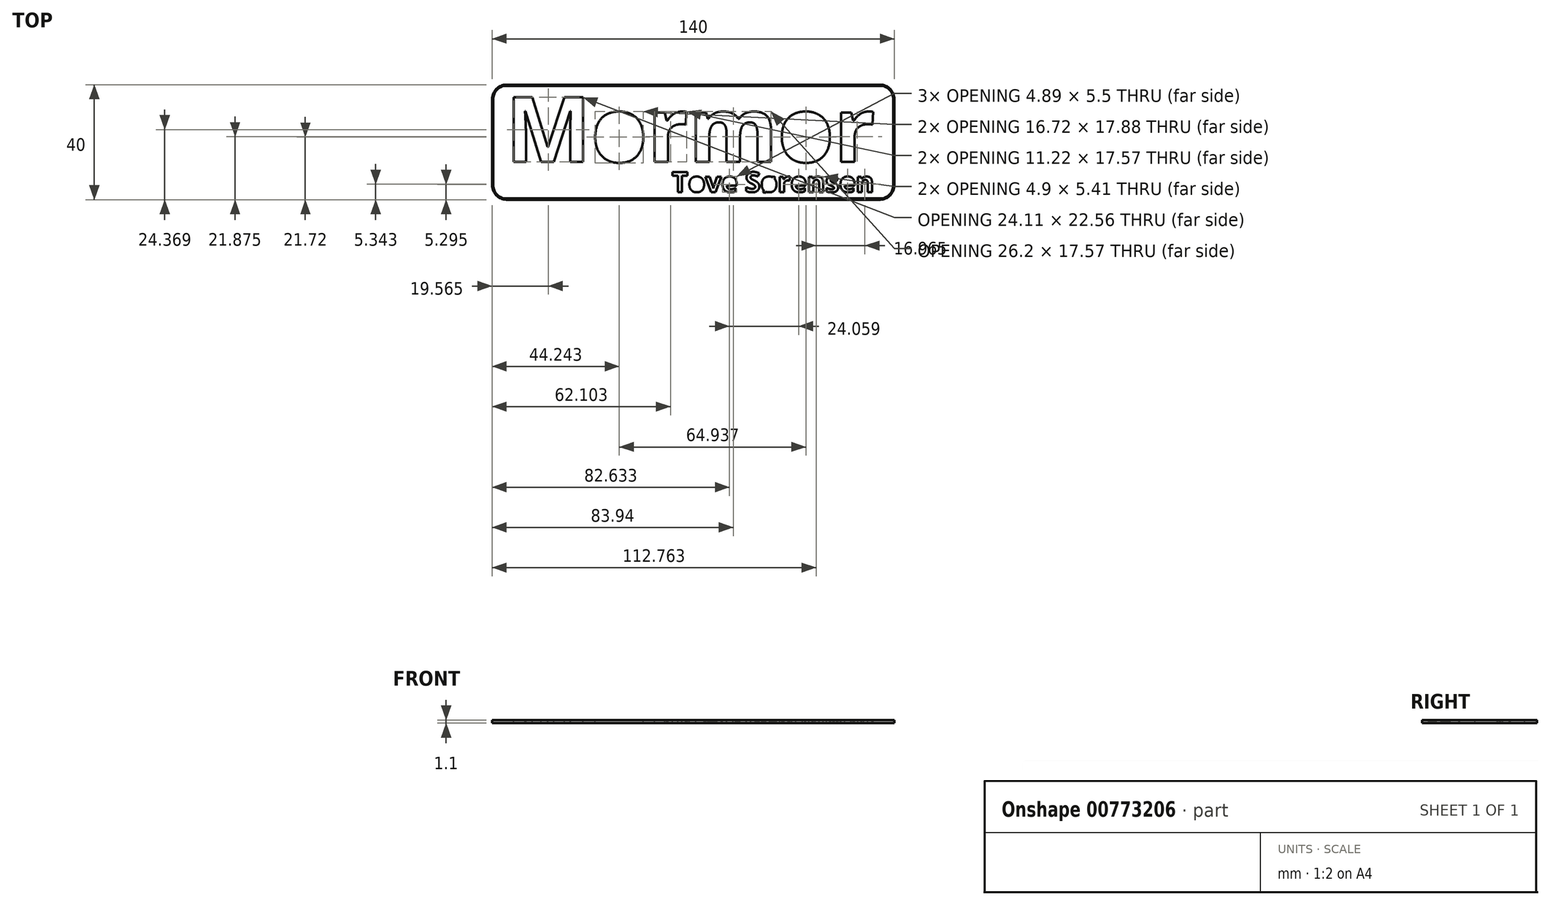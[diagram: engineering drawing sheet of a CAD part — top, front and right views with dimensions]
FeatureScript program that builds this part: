
annotation { "Feature Type Name" : "Feature", "Feature Type Description" : "" }
export const myFeature = defineFeature(function(context is Context, id is Id, definition is map)
    precondition{}
    {
        {
            var Q0;
            Q0=qCreatedBy(makeId("Top.planeOp"),FACE);
            var sketch = newSketch(context, id + "F0", { "sketchPlane" : qUnion([Q0])});
            skLineSegment(sketch, "E0.bottom", {"start": v(-65.25, 40) * mm, "end": v(74.75, 40) * mm});
            skLineSegment(sketch, "E0.top", {"start": v(-65.25, 0) * mm, "end": v(74.75, 0) * mm});
            skLineSegment(sketch, "E0.left", {"start": v(-65.25, 40) * mm, "end": v(-65.25, 0) * mm});
            skLineSegment(sketch, "E0.right", {"start": v(74.75, 40) * mm, "end": v(74.75, 0) * mm});
            skText(sketch, "E1", { "text": "Mormor", "fontName": "OpenSans-Bold.ttf"});
            skText(sketch, "E2", { "text": "Tove Sørensen", "fontName": "OpenSans-Bold.ttf"});
            const initialGuessF0  = {"E1": [-0.06058, 0.01309, 1, 0, 0.02275], "E2": [-0.00268, 0.00264, 1, 0, 0.007]};
            skSetInitialGuess(sketch, initialGuessF0);
            skSolve(sketch);
        }
        {
            var Q0;
            Q0=makeQuery(id+"F0.imprint","IMPRINT",FACE,{"disambiguationData":[TD([[makeQuery(id+"F0.imprint","IMPRINT",EDGE,{"derivedFrom":sQuery(id+"F0.wireOp",EDGE,"E0.bottom")}),-1.0]])]});
            var Q1;
            Q1=makeQuery(id+"F0.imprint","IMPRINT",FACE,{"disambiguationData":[TD([[makeQuery(id+"F0.imprint","IMPRINT",EDGE,{"derivedFrom":sQuery(id+"F0.wireOp",EDGE,"E1.sketch_text.stroke-0")}),1.0]])]});
            extrude(context, id + "F1", {"entities" : qUnion([Q0, Q1]), "oppositeDirection" : true, "depth" : 1 * mm, "offsetDistance" : 25 * mm});
        }
        {
            var Q0;
            Q0=makeQuery(id+"F1.opExtrude","SWEPT_EDGE",EDGE,{"disambiguationData":[OSD([sQuery(id+"F0.wireOp",EDGE,"E0.top"),sQuery(id+"F0.wireOp",EDGE,"E0.right")])]});
            var Q1;
            Q1=makeQuery(id+"F1.opExtrude","SWEPT_EDGE",EDGE,{"disambiguationData":[OSD([sQuery(id+"F0.wireOp",EDGE,"E0.top"),sQuery(id+"F0.wireOp",EDGE,"E0.left")])]});
            var Q2;
            Q2=makeQuery(id+"F1.opExtrude","SWEPT_EDGE",EDGE,{"disambiguationData":[OSD([sQuery(id+"F0.wireOp",EDGE,"E0.bottom"),sQuery(id+"F0.wireOp",EDGE,"E0.left")])]});
            var Q3;
            Q3=makeQuery(id+"F1.opExtrude","SWEPT_EDGE",EDGE,{"disambiguationData":[OSD([sQuery(id+"F0.wireOp",EDGE,"E0.bottom"),sQuery(id+"F0.wireOp",EDGE,"E0.right")])]});
            fillet(context, id + "F2", {"entities" : qUnion([Q0, Q1, Q2, Q3]), "radius" : 5 * mm, "tangentPropagation" : true, "allowEdgeOverflow" : false});
        }
        {
            var Q0;
            Q0=makeQuery(id+"F1.opExtrude","CAP_FACE",FACE,{"disambiguationData":[OSD([sQuery(id+"F0.wireOp",EDGE,"E0.bottom"),sQuery(id+"F0.wireOp",EDGE,"E0.top"),sQuery(id+"F0.wireOp",EDGE,"E0.left"),sQuery(id+"F0.wireOp",EDGE,"E0.right"),sQuery(id+"F0.wireOp",EDGE,"E1.sketch_text.stroke-0"),sQuery(id+"F0.wireOp",EDGE,"E1.sketch_text.stroke-1"),sQuery(id+"F0.wireOp",EDGE,"E1.sketch_text.stroke-2"),sQuery(id+"F0.wireOp",EDGE,"E1.sketch_text.stroke-3"),sQuery(id+"F0.wireOp",EDGE,"E1.sketch_text.stroke-4"),sQuery(id+"F0.wireOp",EDGE,"E1.sketch_text.stroke-5"),sQuery(id+"F0.wireOp",EDGE,"E1.sketch_text.stroke-6"),sQuery(id+"F0.wireOp",EDGE,"E1.sketch_text.stroke-7"),sQuery(id+"F0.wireOp",EDGE,"E1.sketch_text.stroke-8"),sQuery(id+"F0.wireOp",EDGE,"E1.sketch_text.stroke-9"),sQuery(id+"F0.wireOp",EDGE,"E1.sketch_text.stroke-10"),sQuery(id+"F0.wireOp",EDGE,"E1.sketch_text.stroke-11"),sQuery(id+"F0.wireOp",EDGE,"E1.sketch_text.stroke-12"),sQuery(id+"F0.wireOp",EDGE,"E1.sketch_text.stroke-13"),sQuery(id+"F0.wireOp",EDGE,"E1.sketch_text.stroke-14"),sQuery(id+"F0.wireOp",EDGE,"E1.sketch_text.stroke-15"),sQuery(id+"F0.wireOp",EDGE,"E1.sketch_text.stroke-16"),sQuery(id+"F0.wireOp",EDGE,"E1.sketch_text.stroke-17"),sQuery(id+"F0.wireOp",EDGE,"E1.sketch_text.stroke-18"),sQuery(id+"F0.wireOp",EDGE,"E1.sketch_text.stroke-27"),sQuery(id+"F0.wireOp",EDGE,"E1.sketch_text.stroke-28"),sQuery(id+"F0.wireOp",EDGE,"E1.sketch_text.stroke-29"),sQuery(id+"F0.wireOp",EDGE,"E1.sketch_text.stroke-30"),sQuery(id+"F0.wireOp",EDGE,"E1.sketch_text.stroke-31"),sQuery(id+"F0.wireOp",EDGE,"E1.sketch_text.stroke-32"),sQuery(id+"F0.wireOp",EDGE,"E1.sketch_text.stroke-33"),sQuery(id+"F0.wireOp",EDGE,"E1.sketch_text.stroke-34"),sQuery(id+"F0.wireOp",EDGE,"E1.sketch_text.stroke-35"),sQuery(id+"F0.wireOp",EDGE,"E1.sketch_text.stroke-36"),sQuery(id+"F0.wireOp",EDGE,"E1.sketch_text.stroke-37"),sQuery(id+"F0.wireOp",EDGE,"E1.sketch_text.stroke-38"),sQuery(id+"F0.wireOp",EDGE,"E1.sketch_text.stroke-39"),sQuery(id+"F0.wireOp",EDGE,"E1.sketch_text.stroke-40"),sQuery(id+"F0.wireOp",EDGE,"E1.sketch_text.stroke-41"),sQuery(id+"F0.wireOp",EDGE,"E1.sketch_text.stroke-42"),sQuery(id+"F0.wireOp",EDGE,"E1.sketch_text.stroke-43"),sQuery(id+"F0.wireOp",EDGE,"E1.sketch_text.stroke-44"),sQuery(id+"F0.wireOp",EDGE,"E1.sketch_text.stroke-45"),sQuery(id+"F0.wireOp",EDGE,"E1.sketch_text.stroke-46"),sQuery(id+"F0.wireOp",EDGE,"E1.sketch_text.stroke-47"),sQuery(id+"F0.wireOp",EDGE,"E1.sketch_text.stroke-48"),sQuery(id+"F0.wireOp",EDGE,"E1.sketch_text.stroke-49"),sQuery(id+"F0.wireOp",EDGE,"E1.sketch_text.stroke-50"),sQuery(id+"F0.wireOp",EDGE,"E1.sketch_text.stroke-51"),sQuery(id+"F0.wireOp",EDGE,"E1.sketch_text.stroke-52"),sQuery(id+"F0.wireOp",EDGE,"E1.sketch_text.stroke-53"),sQuery(id+"F0.wireOp",EDGE,"E1.sketch_text.stroke-54"),sQuery(id+"F0.wireOp",EDGE,"E1.sketch_text.stroke-55"),sQuery(id+"F0.wireOp",EDGE,"E1.sketch_text.stroke-56"),sQuery(id+"F0.wireOp",EDGE,"E1.sketch_text.stroke-57"),sQuery(id+"F0.wireOp",EDGE,"E1.sketch_text.stroke-58"),sQuery(id+"F0.wireOp",EDGE,"E1.sketch_text.stroke-59"),sQuery(id+"F0.wireOp",EDGE,"E1.sketch_text.stroke-60"),sQuery(id+"F0.wireOp",EDGE,"E1.sketch_text.stroke-61"),sQuery(id+"F0.wireOp",EDGE,"E1.sketch_text.stroke-62"),sQuery(id+"F0.wireOp",EDGE,"E1.sketch_text.stroke-63"),sQuery(id+"F0.wireOp",EDGE,"E1.sketch_text.stroke-64"),sQuery(id+"F0.wireOp",EDGE,"E1.sketch_text.stroke-65"),sQuery(id+"F0.wireOp",EDGE,"E1.sketch_text.stroke-66"),sQuery(id+"F0.wireOp",EDGE,"E1.sketch_text.stroke-67"),sQuery(id+"F0.wireOp",EDGE,"E1.sketch_text.stroke-68"),sQuery(id+"F0.wireOp",EDGE,"E1.sketch_text.stroke-69"),sQuery(id+"F0.wireOp",EDGE,"E1.sketch_text.stroke-70"),sQuery(id+"F0.wireOp",EDGE,"E1.sketch_text.stroke-71"),sQuery(id+"F0.wireOp",EDGE,"E1.sketch_text.stroke-72"),sQuery(id+"F0.wireOp",EDGE,"E1.sketch_text.stroke-73"),sQuery(id+"F0.wireOp",EDGE,"E1.sketch_text.stroke-74"),sQuery(id+"F0.wireOp",EDGE,"E1.sketch_text.stroke-75"),sQuery(id+"F0.wireOp",EDGE,"E1.sketch_text.stroke-76"),sQuery(id+"F0.wireOp",EDGE,"E1.sketch_text.stroke-77"),sQuery(id+"F0.wireOp",EDGE,"E1.sketch_text.stroke-86"),sQuery(id+"F0.wireOp",EDGE,"E1.sketch_text.stroke-87"),sQuery(id+"F0.wireOp",EDGE,"E1.sketch_text.stroke-88"),sQuery(id+"F0.wireOp",EDGE,"E1.sketch_text.stroke-89"),sQuery(id+"F0.wireOp",EDGE,"E1.sketch_text.stroke-90"),sQuery(id+"F0.wireOp",EDGE,"E1.sketch_text.stroke-91"),sQuery(id+"F0.wireOp",EDGE,"E1.sketch_text.stroke-92"),sQuery(id+"F0.wireOp",EDGE,"E1.sketch_text.stroke-93"),sQuery(id+"F0.wireOp",EDGE,"E1.sketch_text.stroke-94"),sQuery(id+"F0.wireOp",EDGE,"E1.sketch_text.stroke-95"),sQuery(id+"F0.wireOp",EDGE,"E1.sketch_text.stroke-96"),sQuery(id+"F0.wireOp",EDGE,"E1.sketch_text.stroke-97"),sQuery(id+"F0.wireOp",EDGE,"E1.sketch_text.stroke-98"),sQuery(id+"F0.wireOp",EDGE,"E1.sketch_text.stroke-99"),sQuery(id+"F0.wireOp",EDGE,"E1.sketch_text.stroke-100"),sQuery(id+"F0.wireOp",EDGE,"E1.sketch_text.stroke-101"),sQuery(id+"F0.wireOp",EDGE,"E1.sketch_text.stroke-102"),sQuery(id+"F0.wireOp",EDGE,"E1.sketch_text.stroke-103"),sQuery(id+"F0.wireOp",EDGE,"E1.sketch_text.stroke-104"),sQuery(id+"F0.wireOp",EDGE,"E1.sketch_text.stroke-105"),sQuery(id+"F0.wireOp",EDGE,"E1.sketch_text.stroke-106"),sQuery(id+"F0.wireOp",EDGE,"E1.sketch_text.stroke-107"),sQuery(id+"F0.wireOp",EDGE,"E1.sketch_text.stroke-108"),sQuery(id+"F0.wireOp",EDGE,"E2.sketch_text.stroke-0"),sQuery(id+"F0.wireOp",EDGE,"E2.sketch_text.stroke-1"),sQuery(id+"F0.wireOp",EDGE,"E2.sketch_text.stroke-2"),sQuery(id+"F0.wireOp",EDGE,"E2.sketch_text.stroke-3"),sQuery(id+"F0.wireOp",EDGE,"E2.sketch_text.stroke-4"),sQuery(id+"F0.wireOp",EDGE,"E2.sketch_text.stroke-5"),sQuery(id+"F0.wireOp",EDGE,"E2.sketch_text.stroke-6"),sQuery(id+"F0.wireOp",EDGE,"E2.sketch_text.stroke-7"),sQuery(id+"F0.wireOp",EDGE,"E2.sketch_text.stroke-16"),sQuery(id+"F0.wireOp",EDGE,"E2.sketch_text.stroke-17"),sQuery(id+"F0.wireOp",EDGE,"E2.sketch_text.stroke-18"),sQuery(id+"F0.wireOp",EDGE,"E2.sketch_text.stroke-19"),sQuery(id+"F0.wireOp",EDGE,"E2.sketch_text.stroke-20"),sQuery(id+"F0.wireOp",EDGE,"E2.sketch_text.stroke-21"),sQuery(id+"F0.wireOp",EDGE,"E2.sketch_text.stroke-22"),sQuery(id+"F0.wireOp",EDGE,"E2.sketch_text.stroke-23"),sQuery(id+"F0.wireOp",EDGE,"E2.sketch_text.stroke-24"),sQuery(id+"F0.wireOp",EDGE,"E2.sketch_text.stroke-25"),sQuery(id+"F0.wireOp",EDGE,"E2.sketch_text.stroke-26"),sQuery(id+"F0.wireOp",EDGE,"E2.sketch_text.stroke-27"),sQuery(id+"F0.wireOp",EDGE,"E2.sketch_text.stroke-28"),sQuery(id+"F0.wireOp",EDGE,"E2.sketch_text.stroke-29"),sQuery(id+"F0.wireOp",EDGE,"E2.sketch_text.stroke-30"),sQuery(id+"F0.wireOp",EDGE,"E2.sketch_text.stroke-31"),sQuery(id+"F0.wireOp",EDGE,"E2.sketch_text.stroke-32"),sQuery(id+"F0.wireOp",EDGE,"E2.sketch_text.stroke-33"),sQuery(id+"F0.wireOp",EDGE,"E2.sketch_text.stroke-34"),sQuery(id+"F0.wireOp",EDGE,"E2.sketch_text.stroke-35"),sQuery(id+"F0.wireOp",EDGE,"E2.sketch_text.stroke-41"),sQuery(id+"F0.wireOp",EDGE,"E2.sketch_text.stroke-42"),sQuery(id+"F0.wireOp",EDGE,"E2.sketch_text.stroke-43"),sQuery(id+"F0.wireOp",EDGE,"E2.sketch_text.stroke-44"),sQuery(id+"F0.wireOp",EDGE,"E2.sketch_text.stroke-45"),sQuery(id+"F0.wireOp",EDGE,"E2.sketch_text.stroke-46"),sQuery(id+"F0.wireOp",EDGE,"E2.sketch_text.stroke-47"),sQuery(id+"F0.wireOp",EDGE,"E2.sketch_text.stroke-48"),sQuery(id+"F0.wireOp",EDGE,"E2.sketch_text.stroke-49"),sQuery(id+"F0.wireOp",EDGE,"E2.sketch_text.stroke-50"),sQuery(id+"F0.wireOp",EDGE,"E2.sketch_text.stroke-51"),sQuery(id+"F0.wireOp",EDGE,"E2.sketch_text.stroke-52"),sQuery(id+"F0.wireOp",EDGE,"E2.sketch_text.stroke-53"),sQuery(id+"F0.wireOp",EDGE,"E2.sketch_text.stroke-54"),sQuery(id+"F0.wireOp",EDGE,"E2.sketch_text.stroke-55"),sQuery(id+"F0.wireOp",EDGE,"E2.sketch_text.stroke-56"),sQuery(id+"F0.wireOp",EDGE,"E2.sketch_text.stroke-57"),sQuery(id+"F0.wireOp",EDGE,"E2.sketch_text.stroke-58"),sQuery(id+"F0.wireOp",EDGE,"E2.sketch_text.stroke-59"),sQuery(id+"F0.wireOp",EDGE,"E2.sketch_text.stroke-60"),sQuery(id+"F0.wireOp",EDGE,"E2.sketch_text.stroke-61"),sQuery(id+"F0.wireOp",EDGE,"E2.sketch_text.stroke-62"),sQuery(id+"F0.wireOp",EDGE,"E2.sketch_text.stroke-63"),sQuery(id+"F0.wireOp",EDGE,"E2.sketch_text.stroke-64"),sQuery(id+"F0.wireOp",EDGE,"E2.sketch_text.stroke-65"),sQuery(id+"F0.wireOp",EDGE,"E2.sketch_text.stroke-66"),sQuery(id+"F0.wireOp",EDGE,"E2.sketch_text.stroke-67"),sQuery(id+"F0.wireOp",EDGE,"E2.sketch_text.stroke-68"),sQuery(id+"F0.wireOp",EDGE,"E2.sketch_text.stroke-69"),sQuery(id+"F0.wireOp",EDGE,"E2.sketch_text.stroke-70"),sQuery(id+"F0.wireOp",EDGE,"E2.sketch_text.stroke-71"),sQuery(id+"F0.wireOp",EDGE,"E2.sketch_text.stroke-72"),sQuery(id+"F0.wireOp",EDGE,"E2.sketch_text.stroke-73"),sQuery(id+"F0.wireOp",EDGE,"E2.sketch_text.stroke-74"),sQuery(id+"F0.wireOp",EDGE,"E2.sketch_text.stroke-75"),sQuery(id+"F0.wireOp",EDGE,"E2.sketch_text.stroke-76"),sQuery(id+"F0.wireOp",EDGE,"E2.sketch_text.stroke-77"),sQuery(id+"F0.wireOp",EDGE,"E2.sketch_text.stroke-78"),sQuery(id+"F0.wireOp",EDGE,"E2.sketch_text.stroke-79"),sQuery(id+"F0.wireOp",EDGE,"E2.sketch_text.stroke-80"),sQuery(id+"F0.wireOp",EDGE,"E2.sketch_text.stroke-81"),sQuery(id+"F0.wireOp",EDGE,"E2.sketch_text.stroke-82"),sQuery(id+"F0.wireOp",EDGE,"E2.sketch_text.stroke-83"),sQuery(id+"F0.wireOp",EDGE,"E2.sketch_text.stroke-84"),sQuery(id+"F0.wireOp",EDGE,"E2.sketch_text.stroke-85"),sQuery(id+"F0.wireOp",EDGE,"E2.sketch_text.stroke-86"),sQuery(id+"F0.wireOp",EDGE,"E2.sketch_text.stroke-87"),sQuery(id+"F0.wireOp",EDGE,"E2.sketch_text.stroke-88"),sQuery(id+"F0.wireOp",EDGE,"E2.sketch_text.stroke-89"),sQuery(id+"F0.wireOp",EDGE,"E2.sketch_text.stroke-90"),sQuery(id+"F0.wireOp",EDGE,"E2.sketch_text.stroke-91"),sQuery(id+"F0.wireOp",EDGE,"E2.sketch_text.stroke-92"),sQuery(id+"F0.wireOp",EDGE,"E2.sketch_text.stroke-93"),sQuery(id+"F0.wireOp",EDGE,"E2.sketch_text.stroke-94"),sQuery(id+"F0.wireOp",EDGE,"E2.sketch_text.stroke-95"),sQuery(id+"F0.wireOp",EDGE,"E2.sketch_text.stroke-96"),sQuery(id+"F0.wireOp",EDGE,"E2.sketch_text.stroke-97"),sQuery(id+"F0.wireOp",EDGE,"E2.sketch_text.stroke-108"),sQuery(id+"F0.wireOp",EDGE,"E2.sketch_text.stroke-109"),sQuery(id+"F0.wireOp",EDGE,"E2.sketch_text.stroke-110"),sQuery(id+"F0.wireOp",EDGE,"E2.sketch_text.stroke-111"),sQuery(id+"F0.wireOp",EDGE,"E2.sketch_text.stroke-112"),sQuery(id+"F0.wireOp",EDGE,"E2.sketch_text.stroke-113"),sQuery(id+"F0.wireOp",EDGE,"E2.sketch_text.stroke-114"),sQuery(id+"F0.wireOp",EDGE,"E2.sketch_text.stroke-115"),sQuery(id+"F0.wireOp",EDGE,"E2.sketch_text.stroke-116"),sQuery(id+"F0.wireOp",EDGE,"E2.sketch_text.stroke-117"),sQuery(id+"F0.wireOp",EDGE,"E2.sketch_text.stroke-118"),sQuery(id+"F0.wireOp",EDGE,"E2.sketch_text.stroke-119"),sQuery(id+"F0.wireOp",EDGE,"E2.sketch_text.stroke-120"),sQuery(id+"F0.wireOp",EDGE,"E2.sketch_text.stroke-126"),sQuery(id+"F0.wireOp",EDGE,"E2.sketch_text.stroke-127"),sQuery(id+"F0.wireOp",EDGE,"E2.sketch_text.stroke-128"),sQuery(id+"F0.wireOp",EDGE,"E2.sketch_text.stroke-129"),sQuery(id+"F0.wireOp",EDGE,"E2.sketch_text.stroke-130"),sQuery(id+"F0.wireOp",EDGE,"E2.sketch_text.stroke-131"),sQuery(id+"F0.wireOp",EDGE,"E2.sketch_text.stroke-132"),sQuery(id+"F0.wireOp",EDGE,"E2.sketch_text.stroke-133"),sQuery(id+"F0.wireOp",EDGE,"E2.sketch_text.stroke-134"),sQuery(id+"F0.wireOp",EDGE,"E2.sketch_text.stroke-135"),sQuery(id+"F0.wireOp",EDGE,"E2.sketch_text.stroke-136"),sQuery(id+"F0.wireOp",EDGE,"E2.sketch_text.stroke-137"),sQuery(id+"F0.wireOp",EDGE,"E2.sketch_text.stroke-138"),sQuery(id+"F0.wireOp",EDGE,"E2.sketch_text.stroke-139"),sQuery(id+"F0.wireOp",EDGE,"E2.sketch_text.stroke-140"),sQuery(id+"F0.wireOp",EDGE,"E2.sketch_text.stroke-141"),sQuery(id+"F0.wireOp",EDGE,"E2.sketch_text.stroke-142"),sQuery(id+"F0.wireOp",EDGE,"E2.sketch_text.stroke-143"),sQuery(id+"F0.wireOp",EDGE,"E2.sketch_text.stroke-144"),sQuery(id+"F0.wireOp",EDGE,"E2.sketch_text.stroke-145"),sQuery(id+"F0.wireOp",EDGE,"E2.sketch_text.stroke-146"),sQuery(id+"F0.wireOp",EDGE,"E2.sketch_text.stroke-147"),sQuery(id+"F0.wireOp",EDGE,"E2.sketch_text.stroke-148"),sQuery(id+"F0.wireOp",EDGE,"E2.sketch_text.stroke-149"),sQuery(id+"F0.wireOp",EDGE,"E2.sketch_text.stroke-150"),sQuery(id+"F0.wireOp",EDGE,"E2.sketch_text.stroke-151"),sQuery(id+"F0.wireOp",EDGE,"E2.sketch_text.stroke-152"),sQuery(id+"F0.wireOp",EDGE,"E2.sketch_text.stroke-153"),sQuery(id+"F0.wireOp",EDGE,"E2.sketch_text.stroke-154"),sQuery(id+"F0.wireOp",EDGE,"E2.sketch_text.stroke-155"),sQuery(id+"F0.wireOp",EDGE,"E2.sketch_text.stroke-156"),sQuery(id+"F0.wireOp",EDGE,"E2.sketch_text.stroke-157"),sQuery(id+"F0.wireOp",EDGE,"E2.sketch_text.stroke-158"),sQuery(id+"F0.wireOp",EDGE,"E2.sketch_text.stroke-159"),sQuery(id+"F0.wireOp",EDGE,"E2.sketch_text.stroke-160"),sQuery(id+"F0.wireOp",EDGE,"E2.sketch_text.stroke-161"),sQuery(id+"F0.wireOp",EDGE,"E2.sketch_text.stroke-162"),sQuery(id+"F0.wireOp",EDGE,"E2.sketch_text.stroke-163"),sQuery(id+"F0.wireOp",EDGE,"E2.sketch_text.stroke-164"),sQuery(id+"F0.wireOp",EDGE,"E2.sketch_text.stroke-165"),sQuery(id+"F0.wireOp",EDGE,"E2.sketch_text.stroke-166"),sQuery(id+"F0.wireOp",EDGE,"E2.sketch_text.stroke-167"),sQuery(id+"F0.wireOp",EDGE,"E2.sketch_text.stroke-168"),sQuery(id+"F0.wireOp",EDGE,"E2.sketch_text.stroke-169"),sQuery(id+"F0.wireOp",EDGE,"E2.sketch_text.stroke-170"),sQuery(id+"F0.wireOp",EDGE,"E2.sketch_text.stroke-171"),sQuery(id+"F0.wireOp",EDGE,"E2.sketch_text.stroke-172"),sQuery(id+"F0.wireOp",EDGE,"E2.sketch_text.stroke-173"),sQuery(id+"F0.wireOp",EDGE,"E2.sketch_text.stroke-174"),sQuery(id+"F0.wireOp",EDGE,"E2.sketch_text.stroke-175"),sQuery(id+"F0.wireOp",EDGE,"E2.sketch_text.stroke-176"),sQuery(id+"F0.wireOp",EDGE,"E2.sketch_text.stroke-177"),sQuery(id+"F0.wireOp",EDGE,"E2.sketch_text.stroke-178"),sQuery(id+"F0.wireOp",EDGE,"E2.sketch_text.stroke-179"),sQuery(id+"F0.wireOp",EDGE,"E2.sketch_text.stroke-180"),sQuery(id+"F0.wireOp",EDGE,"E2.sketch_text.stroke-181"),sQuery(id+"F0.wireOp",EDGE,"E2.sketch_text.stroke-182"),sQuery(id+"F0.wireOp",EDGE,"E2.sketch_text.stroke-183"),sQuery(id+"F0.wireOp",EDGE,"E2.sketch_text.stroke-189"),sQuery(id+"F0.wireOp",EDGE,"E2.sketch_text.stroke-190"),sQuery(id+"F0.wireOp",EDGE,"E2.sketch_text.stroke-191"),sQuery(id+"F0.wireOp",EDGE,"E2.sketch_text.stroke-192"),sQuery(id+"F0.wireOp",EDGE,"E2.sketch_text.stroke-193"),sQuery(id+"F0.wireOp",EDGE,"E2.sketch_text.stroke-194"),sQuery(id+"F0.wireOp",EDGE,"E2.sketch_text.stroke-195"),sQuery(id+"F0.wireOp",EDGE,"E2.sketch_text.stroke-196"),sQuery(id+"F0.wireOp",EDGE,"E2.sketch_text.stroke-197"),sQuery(id+"F0.wireOp",EDGE,"E2.sketch_text.stroke-198"),sQuery(id+"F0.wireOp",EDGE,"E2.sketch_text.stroke-199"),sQuery(id+"F0.wireOp",EDGE,"E2.sketch_text.stroke-200"),sQuery(id+"F0.wireOp",EDGE,"E2.sketch_text.stroke-201"),sQuery(id+"F0.wireOp",EDGE,"E2.sketch_text.stroke-202"),sQuery(id+"F0.wireOp",EDGE,"E2.sketch_text.stroke-203"),sQuery(id+"F0.wireOp",EDGE,"E2.sketch_text.stroke-204"),sQuery(id+"F0.wireOp",EDGE,"E2.sketch_text.stroke-205"),sQuery(id+"F0.wireOp",EDGE,"E2.sketch_text.stroke-206"),sQuery(id+"F0.wireOp",EDGE,"E2.sketch_text.stroke-207"),sQuery(id+"F0.wireOp",EDGE,"E2.sketch_text.stroke-208"),sQuery(id+"F0.wireOp",EDGE,"E2.sketch_text.stroke-209"),sQuery(id+"F0.wireOp",EDGE,"E2.sketch_text.stroke-210"),sQuery(id+"F0.wireOp",EDGE,"E2.sketch_text.stroke-211"),sQuery(id+"F0.wireOp",EDGE,"E2.sketch_text.stroke-212"),sQuery(id+"F0.wireOp",EDGE,"E2.sketch_text.stroke-213"),sQuery(id+"F0.wireOp",EDGE,"E2.sketch_text.stroke-214"),sQuery(id+"F0.wireOp",EDGE,"E2.sketch_text.stroke-215"),sQuery(id+"F0.wireOp",EDGE,"E2.sketch_text.stroke-216"),sQuery(id+"F0.wireOp",EDGE,"E2.sketch_text.stroke-217"),sQuery(id+"F0.wireOp",EDGE,"E2.sketch_text.stroke-218"),sQuery(id+"F0.wireOp",EDGE,"E2.sketch_text.stroke-219"),sQuery(id+"F0.wireOp",EDGE,"E2.sketch_text.stroke-220")])],"isStart":true});
            var sketch = newSketch(context, id + "F3", { "sketchPlane" : qUnion([Q0])});
            skLineSegment(sketch, "E3.0", {"start": v(-60.25, 39.6) * mm, "end": v(69.75, 39.6) * mm});
            skArc(sketch, "E3.1", {"start": v(74.35, 35) * mm, "mid": v(73, 38.25) * mm, "end": v(69.75, 39.6) * mm});
            skArc(sketch, "E3.2", {"start": v(-60.25, 39.6) * mm, "mid": v(-63.5, 38.25) * mm, "end": v(-64.85, 35) * mm});
            skLineSegment(sketch, "E3.3", {"start": v(74.35, 35) * mm, "end": v(74.35, 5) * mm});
            skLineSegment(sketch, "E3.4", {"start": v(-64.85, 35) * mm, "end": v(-64.85, 5) * mm});
            skArc(sketch, "E3.5", {"start": v(-64.85, 5) * mm, "mid": v(-63.5, 1.75) * mm, "end": v(-60.25, 0.4) * mm});
            skLineSegment(sketch, "E3.6", {"start": v(-60.25, 0.4) * mm, "end": v(69.75, 0.4) * mm});
            skArc(sketch, "E3.7", {"start": v(69.75, 0.4) * mm, "mid": v(73, 1.75) * mm, "end": v(74.35, 5) * mm});
            skSolve(sketch);
        }
        {
            var Q0;
            Q0=makeQuery(id+"F3.imprint","IMPRINT",FACE,{"disambiguationData":[TD([[makeQuery(id+"F3.imprint","IMPRINT",EDGE,{"derivedFrom":sQuery(id+"F3.wireOp",EDGE,"E3.0")}),1.0]])]});
            extrude(context, id + "F4", {"entities" : qUnion([Q0]), "operationType" : NewBodyOperationType.ADD, "depth" : 0.1 * mm, "offsetDistance" : 25 * mm});
        }
    });
